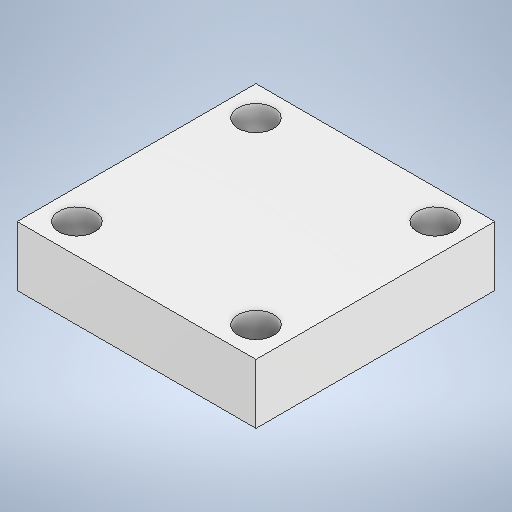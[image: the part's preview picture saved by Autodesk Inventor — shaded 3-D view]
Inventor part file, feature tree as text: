
AUTODESK INVENTOR PART (.ipt)
format: ipt  version: 2025.3 (Build 293356000, 356)  size: 222,208 bytes
history: native  units: mm
features: extrude x3, sketch x3, other x1
ambient origin geometry x8: Origin, YZ Plane, XZ Plane, XY Plane, X Axis, Y Axis, Z Axis, Center Point
bodies: Body1 (feature_tree)
feature tree (7):
  other  "Sólido1"
  extrude  "Extrusión1"  Depth=20.0mm
  extrude  "Extrusión2"  Depth=5.0mm
  extrude  "Extrusión3"  Depth=5.0mm
  sketch  "Boceto1"  dims[d0=20.0mm d1=20.0mm]
  sketch  "Boceto2"  dims[d2=5.0mm d3=0.0mm d4=6.0mm]
  sketch  "Boceto3"  dims[d5=2.5mm d6=0.0mm d7=15.0mm d8=15.0mm d9=3.0mm d10=3.0mm d11=3.0mm d12=3.0mm d13=5.0mm d14=0.0mm]
